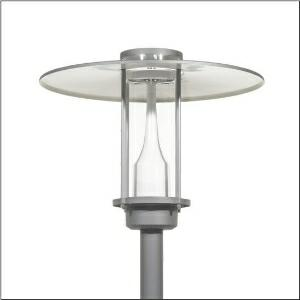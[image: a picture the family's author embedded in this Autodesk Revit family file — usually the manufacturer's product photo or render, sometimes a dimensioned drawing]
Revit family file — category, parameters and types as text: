
# Revit family: city-light_plus_iq___pl1_2s_5xa5275of14h_1ed9
name_source: partatom
category: Lighting Fixtures
units: mm (PartAtom-declared; Revit-internal decimal feet)

## family parameters
Cut with Voids When Loaded = No
Host = Face
Light Source = No
Part Type = Normal
Room Calculation Point = No
Round Connector Dimension = Use Diameter
Shared = No

## types (1)
- --- (1 x LED, 2840 lm, 21.8 W, 2700K)
    Apparent Load = 22 VA
    CIE Flux Codes = 23 63 93 97 100
    Color Rendering = 70
    Color Temperature = 2700K
    Default Elevation = 1800 mm
    Description = City-Light Plus iQ, mast luminaire, Module 540 iQ-SR, primary light control with 3 zone facetted reflector, of plastic, silver coated, highly specular, structured, primary optical cover: cover, of PMMA, transparent, light distribution: PL1.2s, light emission: direct distribution, primary light characteristic: symmetric, installation type: post-top, LED, High Power LED, rated luminous flux: 2.840lm, luminous efficacy: 130lm/W, light colour: 727, colour temperature: 2700K, control gear: iQ Street-Remote, control: pre-setting: logarithmic dimming characteristic, Street-Remote, Auto-Match, Temp-Guard, Lumen-Switch, Night-Set, Smart-Wire, Light-Fading, Desk-Remote (wireless, voltage-free reading and setting of iQ features in the workshop via application-optimized NFC function/RFID function), optimised constant luminous flux control (CLO 2.0), with terminal, 6-pole, max. 2.5mm², mains connection: 230..240V, AC, 50/60Hz, start of lifetime: 22W, end of service life: 23W, reduction: 11W, luminaire housing, upper part, of glass-fibre reinforced polyester, coated, Siteco® metallic grey (DB 702S), diameter: 750mm, height: 590mm, spigot size: d x l = 76 x 70mm (post-top) | with reducer (optional accessory) 60 x 70mm, mounting height: 3..5m, post-top mast mounting element, of diecast aluminium, coated, Siteco® metallic grey (DB 702S), Module 540 iQ-SR, traffic white (RAL 9016), equipment: standard, protection rating (complete): IP65, insulation class (complete): insulation class II (safety insulation), certification: CE, ENEC, VDE, packaging unit: 1 piece

Light Distribution: PL1.2s
    Height = 590 mm
    Lamp = 1 x LED
    Lamp Light Flux = 2840 lm
    Lamp Power = 21.8 W
    Lamp count = 1
    Length = 750 mm
    Luminous efficacy = 130 lm/W
    Manufacturer = Siteco
    ModVariant = No
    Model = 5XA5275OF14H
    Number of Poles = 1
    OnlyDefault = Yes
    Power Factor = 1
    Product Name = City-Light Plus iQ | PL1.2s
    Product group = mast luminaire | pylon top
    ProductGroupID = 6100
    Protection Class = Protection class II
    Protection Degree = IP 65
    RLX_Detail_Level = 1
    RLX_Emergency_Light_Flux = 0 lm
    RLX_Emergency_Type = 0
    RLX_Emergency_Type_DB = No
    RlxData = <blob elided: 33161 chars, md5=71ed884b>
    Socket = socket
    Standby Power = 0 W
    System Light Flux = 2840 lm
    System Power = 22 W
    Type Comments = factory setting: luminous flux: 100 % | dim-lin: 254 | 456 mA
    Type Image = l_1006456.jpg
    URL = http://relux.com
    VarID = @adj_166929
    Voltage = 0 V
    Weight = 0.00 kg
    Width = 0 mm  [stored 0 ft]

note: [stored X ft] marks values corroborated as IEEE doubles in the binary element streams (Revit-internal decimal feet)

## geometry (parser evidence)
native form markers: Blend x4, Sweep x11
no freeform markers — native parametric forms only
